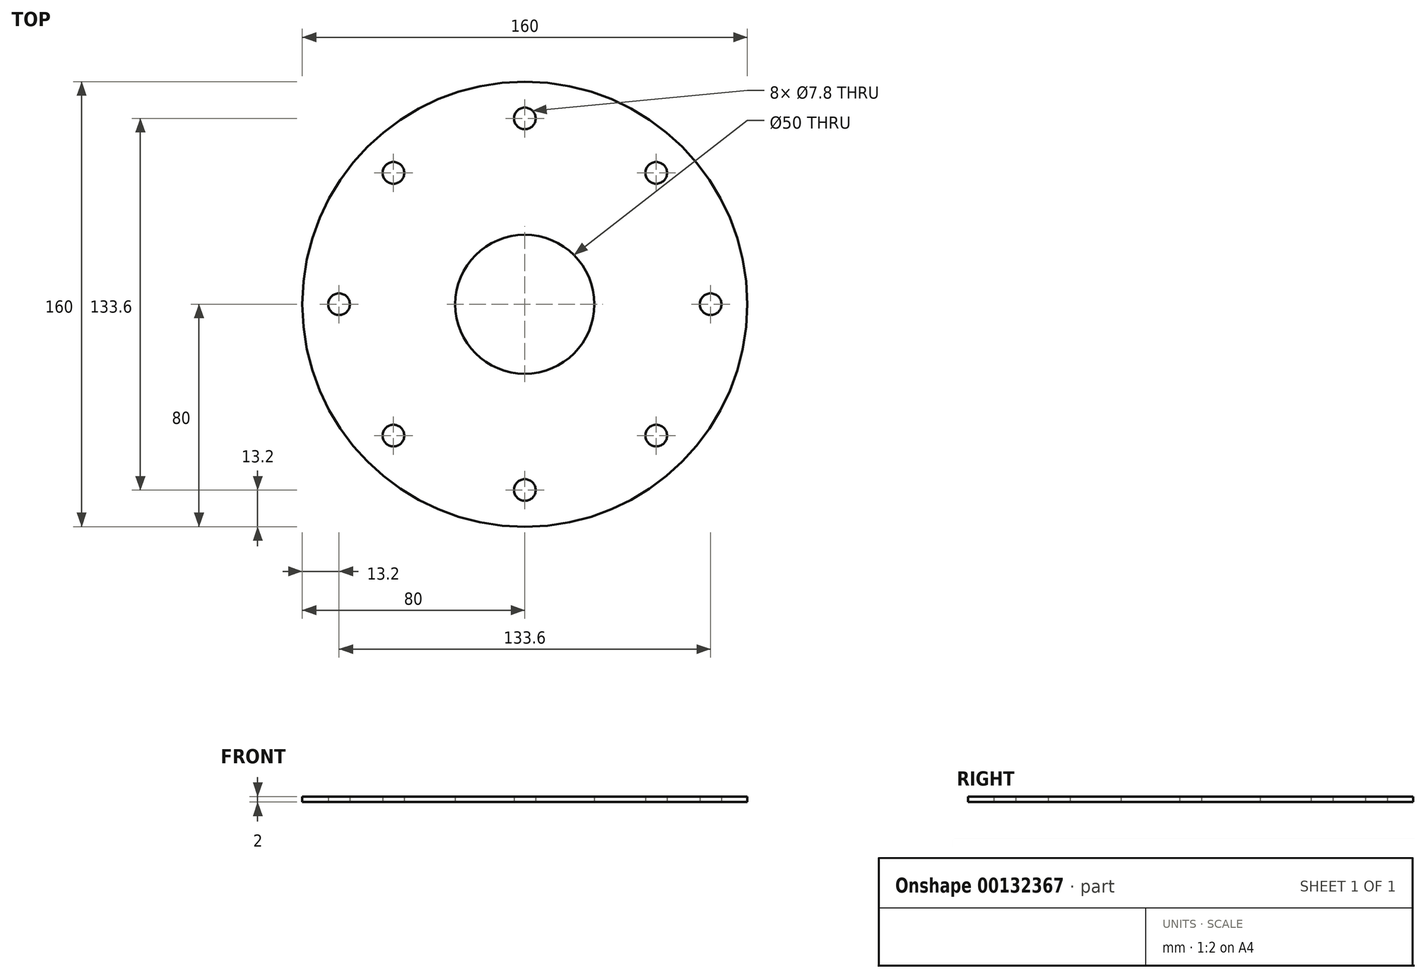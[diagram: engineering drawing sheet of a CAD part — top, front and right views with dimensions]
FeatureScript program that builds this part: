
annotation { "Feature Type Name" : "Feature", "Feature Type Description" : "" }
export const myFeature = defineFeature(function(context is Context, id is Id, definition is map)
    precondition{}
    {
        {
            var Q0;
            Q0=qCreatedBy(makeId("Top.planeOp"),FACE);
            var sketch = newSketch(context, id + "F0", { "sketchPlane" : qUnion([Q0])});
            skCircle(sketch, "E0", {"center": v(0, 0) * mm, "radius": 80 * mm});
            skCircle(sketch, "E1", {"center": v(0, 66.8) * mm, "radius": 3.9 * mm});
            skCircle(sketch, "E2", {"center": v(0, 0) * mm, "radius": 25 * mm});
            skCircle(sketch, "E3.1.0", {"center": v(-47.23, 47.23) * mm, "radius": 3.9 * mm});
            skCircle(sketch, "E3.2.0", {"center": v(-66.8, 0) * mm, "radius": 3.9 * mm});
            skCircle(sketch, "E3.3.0", {"center": v(-47.23, -47.23) * mm, "radius": 3.9 * mm});
            skCircle(sketch, "E3.4.0", {"center": v(0, -66.8) * mm, "radius": 3.9 * mm});
            skCircle(sketch, "E3.5.0", {"center": v(47.23, -47.23) * mm, "radius": 3.9 * mm});
            skCircle(sketch, "E3.6.0", {"center": v(66.8, 0) * mm, "radius": 3.9 * mm});
            skCircle(sketch, "E3.7.0", {"center": v(47.23, 47.23) * mm, "radius": 3.9 * mm});
            skSolve(sketch);
        }
        {
            var Q0;
            Q0 = qSketchRegion(id + "F0", true);
            extrude(context, id + "F1", {"entities" : qUnion([Q0]), "depth" : 2 * mm});
        }
    });
